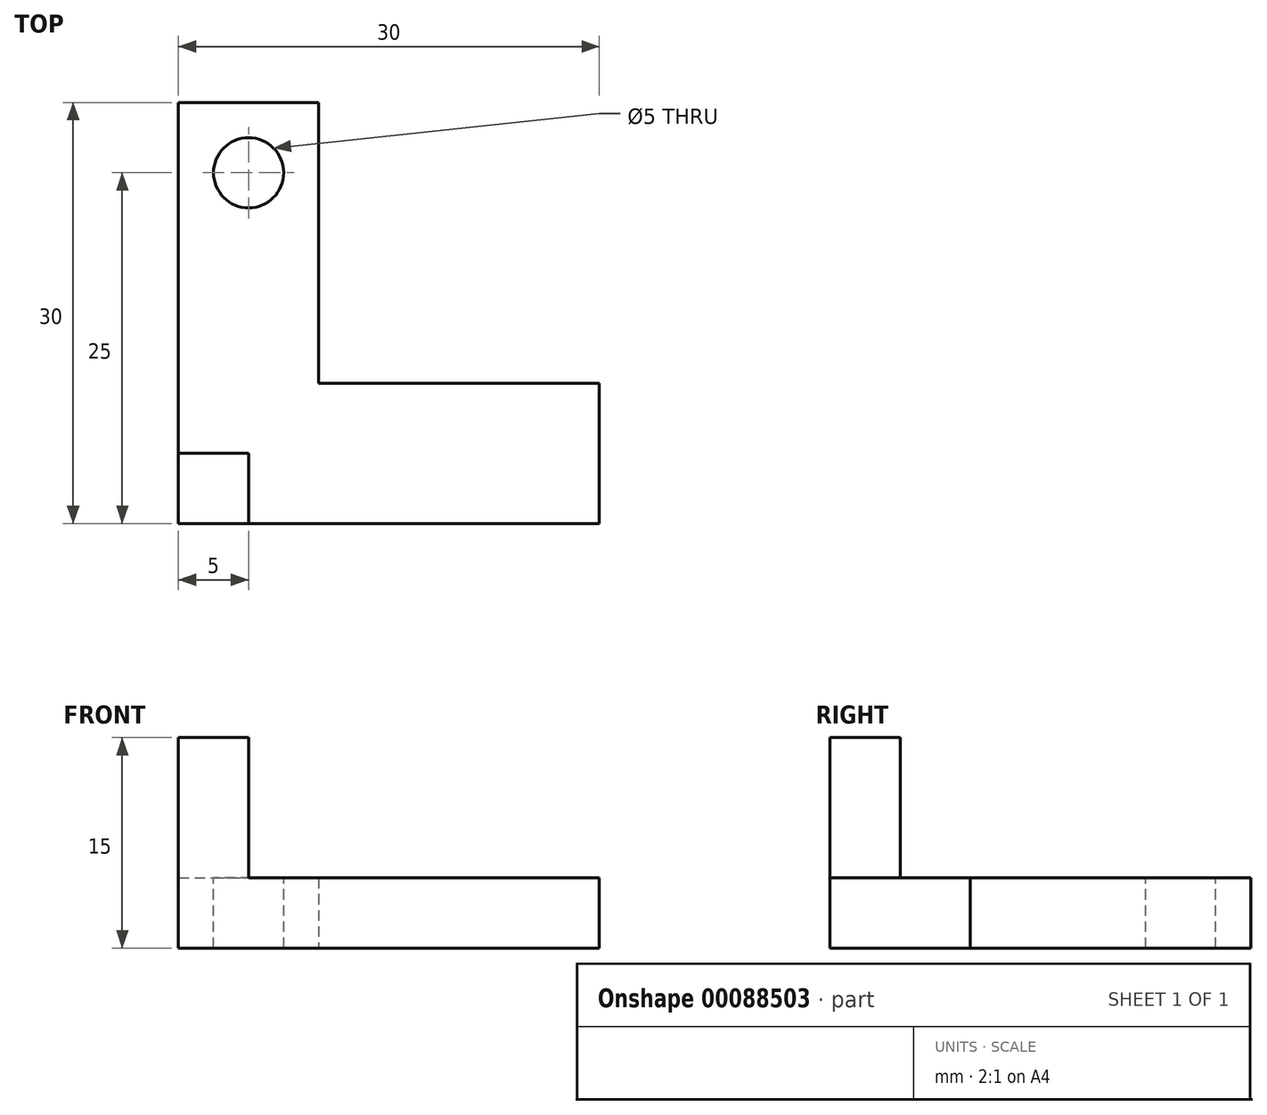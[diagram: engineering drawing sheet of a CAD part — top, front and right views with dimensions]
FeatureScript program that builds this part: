
annotation { "Feature Type Name" : "Feature", "Feature Type Description" : "" }
export const myFeature = defineFeature(function(context is Context, id is Id, definition is map)
    precondition{}
    {
        {
            var Q0;
            Q0=qCreatedBy(makeId("Top.planeOp"),FACE);
            var sketch = newSketch(context, id + "F0", { "sketchPlane" : qUnion([Q0])});
            skLineSegment(sketch, "E0.bottom", {"start": v(15, -15) * mm, "end": v(-15, -15) * mm});
            skLineSegment(sketch, "E0.top", {"start": v(-5, 15) * mm, "end": v(-15, 15) * mm});
            skLineSegment(sketch, "E0.left", {"start": v(15, -15) * mm, "end": v(15, -5) * mm});
            skLineSegment(sketch, "E0.right", {"start": v(-15, -15) * mm, "end": v(-15, 15) * mm});
            skPoint(sketch, "E0.middle", {"position": v(0, 0) * mm});
            skLineSegment(sketch, "E1.top", {"start": v(15, -5) * mm, "end": v(-5, -5) * mm});
            skLineSegment(sketch, "E1.right", {"start": v(-5, 15) * mm, "end": v(-5, -5) * mm});
            skPoint(sketch, "E2.orphan", {"position": v(15, 15) * mm});
            skSolve(sketch);
        }
        {
            var Q0;
            Q0=makeQuery(id+"F0.imprint","IMPRINT",FACE,{"disambiguationData":[TD([[makeQuery(id+"F0.imprint","IMPRINT",EDGE,{"derivedFrom":sQuery(id+"F0.wireOp",EDGE,"E0.bottom")}),-1.0]])]});
            extrude(context, id + "F1", {"entities" : qUnion([Q0]), "depth" : 5 * mm});
        }
        {
            var Q0;
            Q0=makeQuery(id+"F1.opExtrude","CAP_FACE",FACE,{"disambiguationData":[OSD([sQuery(id+"F0.wireOp",EDGE,"E0.bottom"),sQuery(id+"F0.wireOp",EDGE,"E0.top"),sQuery(id+"F0.wireOp",EDGE,"E0.left"),sQuery(id+"F0.wireOp",EDGE,"E0.right"),sQuery(id+"F0.wireOp",EDGE,"E1.top"),sQuery(id+"F0.wireOp",EDGE,"E1.right")])],"isStart":false});
            var sketch = newSketch(context, id + "F2", { "sketchPlane" : qUnion([Q0])});
            skLineSegment(sketch, "E3.bottom", {"start": v(-15, -15) * mm, "end": v(-10, -15) * mm});
            skLineSegment(sketch, "E3.top", {"start": v(-15, -10) * mm, "end": v(-10, -10) * mm});
            skLineSegment(sketch, "E3.left", {"start": v(-15, -15) * mm, "end": v(-15, -10) * mm});
            skLineSegment(sketch, "E3.right", {"start": v(-10, -15) * mm, "end": v(-10, -10) * mm});
            skSolve(sketch);
        }
        {
            var Q0;
            Q0=makeQuery(id+"F2.imprint","IMPRINT",FACE,{"disambiguationData":[TD([[makeQuery(id+"F2.imprint","IMPRINT",EDGE,{"derivedFrom":sQuery(id+"F2.wireOp",EDGE,"E3.bottom")}),-1.0]])]});
            extrude(context, id + "F3", {"entities" : qUnion([Q0]), "operationType" : NewBodyOperationType.ADD, "depth" : 10 * mm});
        }
        {
            var Q0;
            Q0=makeQuery(id+"F1.opExtrude","CAP_FACE",FACE,{"disambiguationData":[OSD([sQuery(id+"F0.wireOp",EDGE,"E0.bottom"),sQuery(id+"F0.wireOp",EDGE,"E0.top"),sQuery(id+"F0.wireOp",EDGE,"E0.left"),sQuery(id+"F0.wireOp",EDGE,"E0.right"),sQuery(id+"F0.wireOp",EDGE,"E1.top"),sQuery(id+"F0.wireOp",EDGE,"E1.right")])],"isStart":false});
            var sketch = newSketch(context, id + "F4", { "sketchPlane" : qUnion([Q0])});
            skLineSegment(sketch, "E4.bottom", {"start": v(-15, 15) * mm, "end": v(-5, 15) * mm});
            skLineSegment(sketch, "E4.top", {"start": v(-15, 5) * mm, "end": v(-5, 5) * mm});
            skLineSegment(sketch, "E4.left", {"start": v(-15, 15) * mm, "end": v(-15, 5) * mm});
            skLineSegment(sketch, "E4.right", {"start": v(-5, 15) * mm, "end": v(-5, 5) * mm});
            skLineSegment(sketch, "E5", {"start": v(-15, 15) * mm, "end": v(-5, 5) * mm});
            skLineSegment(sketch, "E6", {"start": v(-5, 15) * mm, "end": v(-15, 5) * mm});
            skPoint(sketch, "E7", {"position": v(-10, 10) * mm});
            skSolve(sketch);
        }
        {
            var Q0;
            Q0=sQuery(id+"F4.wireOp",VERTEX,"E7");
            var Q1;
            Q1=makeQuery(id+"F1.opExtrude","SWEPT_BODY",BODY,{"disambiguationData":[OSD([sQuery(id+"F0.wireOp",EDGE,"E0.bottom"),sQuery(id+"F0.wireOp",EDGE,"E0.top"),sQuery(id+"F0.wireOp",EDGE,"E0.left"),sQuery(id+"F0.wireOp",EDGE,"E0.right"),sQuery(id+"F0.wireOp",EDGE,"E1.top"),sQuery(id+"F0.wireOp",EDGE,"E1.right")])]});
            hole(context, id + "F5", {"style" : HoleStyle.SIMPLE, "endStyle" : HoleEndStyle.THROUGH, "holeDiameter" : 5 * mm, "locations" : qUnion([Q0]), "scope" : qUnion([Q1]), "isTappedThrough" : true});
        }
    });
